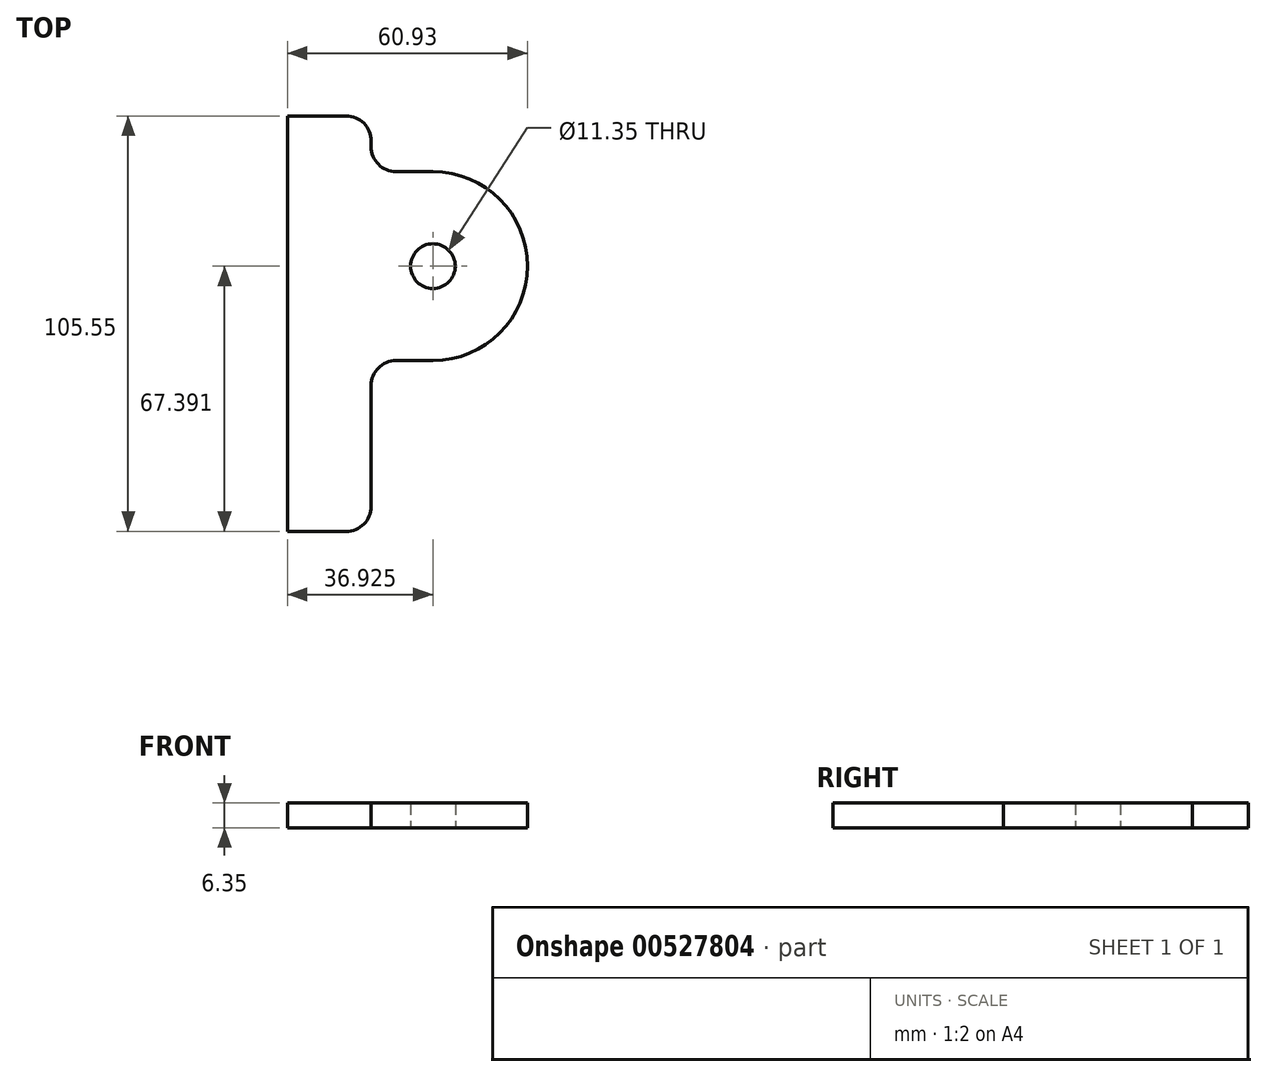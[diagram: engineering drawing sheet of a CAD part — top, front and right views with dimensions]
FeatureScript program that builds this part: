
annotation { "Feature Type Name" : "Feature", "Feature Type Description" : "" }
export const myFeature = defineFeature(function(context is Context, id is Id, definition is map)
    precondition{}
    {
        {
            var Q0;
            Q0=qCreatedBy(makeId("Top.planeOp"),FACE);
            var sketch = newSketch(context, id + "F0", { "sketchPlane" : qUnion([Q0])});
            skLineSegment(sketch, "E0.bottom", {"start": v(-31.54, 48.93) * mm, "end": v(-16.66, 48.93) * mm});
            skLineSegment(sketch, "E0.top", {"start": v(-31.54, -56.62) * mm, "end": v(-16.66, -56.62) * mm});
            skLineSegment(sketch, "E0.left", {"start": v(-31.54, 48.93) * mm, "end": v(-31.54, -56.62) * mm});
            skLineSegment(sketch, "E0.right", {"start": v(-10.3, 42.58) * mm, "end": v(-10.3, 41.13) * mm});
            skCircle(sketch, "E1", {"center": v(5.39, 10.77) * mm, "radius": 24 * mm});
            skLineSegment(sketch, "E2", {"start": v(5.39, 34.78) * mm, "end": v(-3.96, 34.78) * mm});
            skLineSegment(sketch, "E3", {"start": v(5.39, -13.23) * mm, "end": v(-3.96, -13.23) * mm});
            skArc(sketch, "E4.filletArc", {"start": v(-10.3, 41.13) * mm, "mid": v(-8.45, 36.64) * mm, "end": v(-3.96, 34.78) * mm});
            skPoint(sketch, "E5.visualSharp", {"position": v(-10.3, 48.93) * mm});
            skArc(sketch, "E5.filletArc", {"start": v(-10.3, 42.58) * mm, "mid": v(-12.17, 47.07) * mm, "end": v(-16.66, 48.93) * mm});
            skLineSegment(sketch, "E6", {"start": v(-10.3, -19.58) * mm, "end": v(-10.3, -50.27) * mm});
            skPoint(sketch, "E7.visualSharp", {"position": v(-10.3, -13.23) * mm});
            skArc(sketch, "E7.filletArc", {"start": v(-3.96, -13.23) * mm, "mid": v(-8.45, -15.1) * mm, "end": v(-10.3, -19.58) * mm});
            skPoint(sketch, "E8.visualSharp", {"position": v(-10.3, -56.62) * mm});
            skArc(sketch, "E8.filletArc", {"start": v(-16.66, -56.62) * mm, "mid": v(-12.17, -54.76) * mm, "end": v(-10.3, -50.27) * mm});
            skCircle(sketch, "E9", {"center": v(5.39, 10.77) * mm, "radius": 5.67 * mm});
            skSolve(sketch);
        }
        {
            var Q0;
            Q0=makeQuery(id+"F0.imprint","IMPRINT",FACE,{"disambiguationData":[TD([[makeQuery(id+"F0.imprint","IMPRINT",EDGE,{"derivedFrom":sQuery(id+"F0.wireOp",EDGE,"E9")}),-1.0]])]});
            var Q1;
            Q1=makeQuery(id+"F0.imprint","IMPRINT",FACE,{"disambiguationData":[TD([[makeQuery(id+"F0.imprint","IMPRINT",EDGE,{"derivedFrom":sQuery(id+"F0.wireOp",EDGE,"E0.bottom")}),-1.0]])]});
            extrude(context, id + "F1", {"entities" : qUnion([Q0, Q1]), "depth" : 6.35 * mm, "offsetDistance" : 25.4 * mm});
        }
    });
